# Revit family: p_system_a-k_pn60-110
name_source: partatom
category: Drzwi
revit_build: Autodesk Revit 2016 (Build: 20150714_1515(x64)
units: mm (PartAtom-declared; Revit-internal decimal feet)

## family parameters
Obiekt nadrzędny = Ściana
Punkt obliczania pomieszczeń = Nie
Tnij formami wycięć po wczytaniu = Nie
Współdzielony = Nie
Zawsze pionowo = Tak

## types (6) — shared parameters
Funkcja = Wewnętrzna
Konstrukcja analityczna = <Brak>
Model = Porta SYSTEM
Opis = Własność Porta KMI Poland, wszelkie prawa zastrzeżone.
Producent = PORTA KMI POLAND
URL = www.porta.com.pl
Wysokość = 2016 mm
Wysokość brutto = 2060 mm  [stored 6.75853 ft]
Zakończenie ściany = Wg obiektu nadrzędnego

## per-type parameters (varying)
| type | Sb | Szerokość | Szerokość brutto |
| PN 70 | 746 mm | 700 mm | 780 mm |
| PN 60 | 646 mm | 600 mm | 680 mm |
| PN 80 | 846 mm | 800 mm | 880 mm  [stored 2.88714 ft] |
| PN 90 | 946 mm | 900 mm | 980 mm |
| PN 100 | 1046 mm | 1000 mm  [stored 3.28084 ft] | 1080 mm |
| PN 110 | 1146 mm | 1100 mm | 1180 mm |

note: [stored X ft] marks values corroborated as IEEE doubles in the binary element streams (Revit-internal decimal feet)

## geometry (parser evidence)
native form markers: Blend x2
no freeform markers — native parametric forms only
